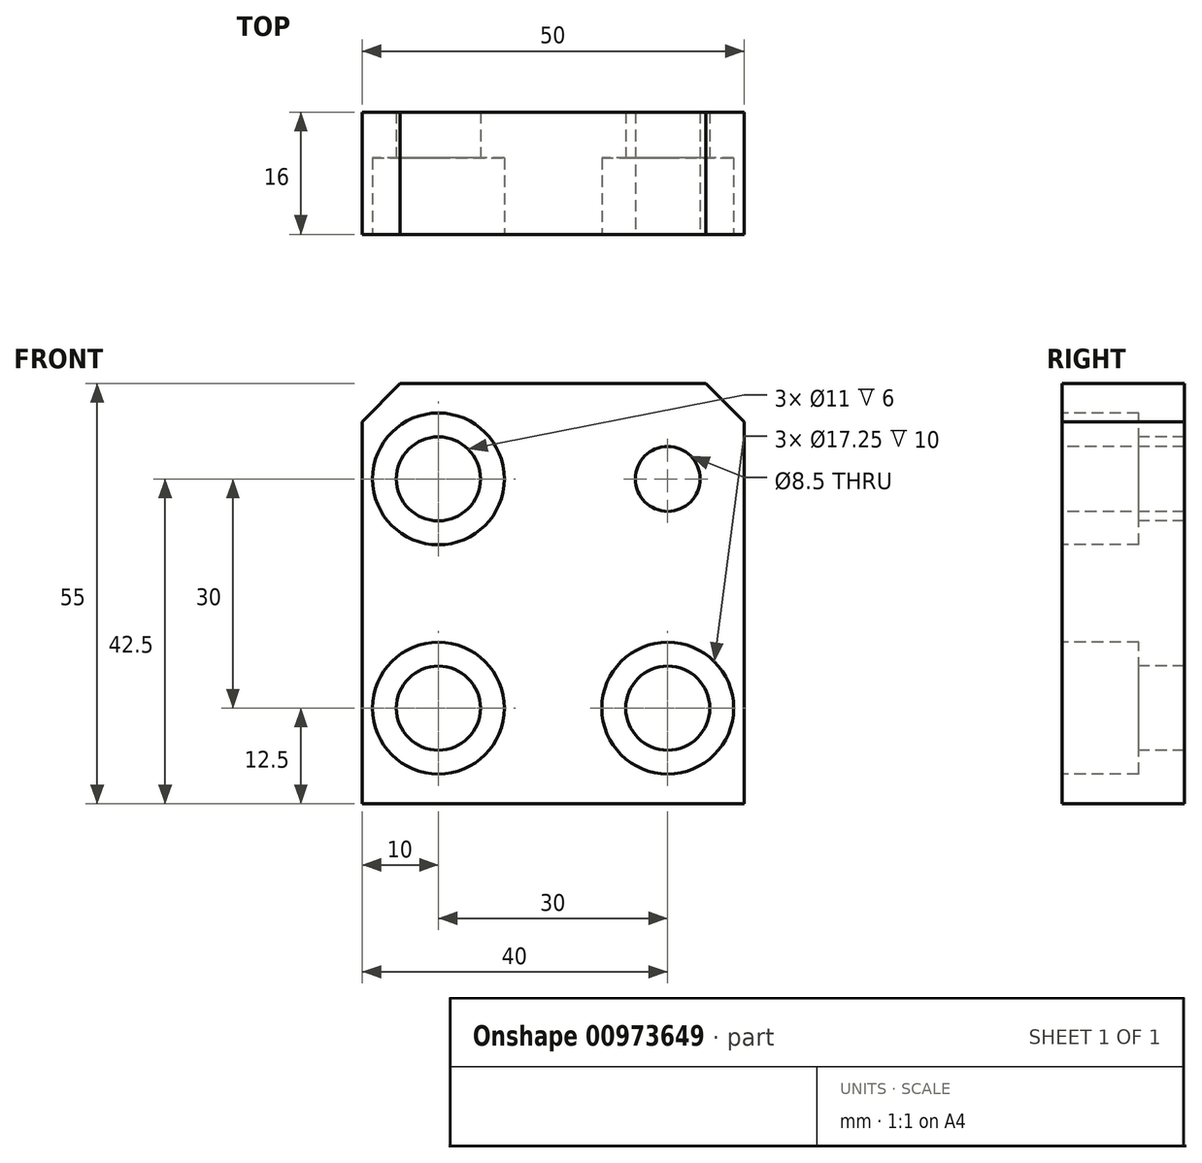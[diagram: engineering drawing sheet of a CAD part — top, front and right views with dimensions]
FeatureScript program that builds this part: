
annotation { "Feature Type Name" : "Feature", "Feature Type Description" : "" }
export const myFeature = defineFeature(function(context is Context, id is Id, definition is map)
    precondition{}
    {
        {
            var Q0;
            Q0=qCreatedBy(makeId("Front.planeOp"),FACE);
            var sketch = newSketch(context, id + "F0", { "sketchPlane" : qUnion([Q0])});
            skLineSegment(sketch, "E0.bottom", {"start": v(-25, -27.5) * mm, "end": v(25, -27.5) * mm});
            skLineSegment(sketch, "E0.top", {"start": v(-25, 27.5) * mm, "end": v(25, 27.5) * mm});
            skLineSegment(sketch, "E0.left", {"start": v(-25, -27.5) * mm, "end": v(-25, 27.5) * mm});
            skLineSegment(sketch, "E0.right", {"start": v(25, -27.5) * mm, "end": v(25, 27.5) * mm});
            skSolve(sketch);
        }
        {
            var Q0;
            Q0 = qSketchRegion(id + "F0", true);
            extrude(context, id + "F1", {"entities" : qUnion([Q0]), "oppositeDirection" : true, "depth" : 16 * mm, "offsetDistance" : 25.4 * mm});
        }
        {
            var Q0;
            Q0=makeQuery(id+"F1.opExtrude","CAP_FACE",FACE,{"disambiguationData":[OSD([sQuery(id+"F0.wireOp",EDGE,"E0.bottom"),sQuery(id+"F0.wireOp",EDGE,"E0.top"),sQuery(id+"F0.wireOp",EDGE,"E0.left"),sQuery(id+"F0.wireOp",EDGE,"E0.right")])],"isStart":true});
            var sketch = newSketch(context, id + "F2", { "sketchPlane" : qUnion([Q0])});
            skPoint(sketch, "E1", {"position": v(-15, 15) * mm});
            skPoint(sketch, "E2", {"position": v(-15, -15) * mm});
            skPoint(sketch, "E3", {"position": v(15, -15) * mm});
            skSolve(sketch);
        }
        {
            var Q0;
            Q0=sQuery(id+"F2.wireOp",VERTEX,"E1");
            var Q1;
            Q1=sQuery(id+"F2.wireOp",VERTEX,"E2");
            var Q2;
            Q2=sQuery(id+"F2.wireOp",VERTEX,"E3");
            var Q3;
            Q3=makeQuery(id+"F1.opExtrude","SWEPT_BODY",BODY,{"disambiguationData":[OSD([sQuery(id+"F0.wireOp",EDGE,"E0.bottom"),sQuery(id+"F0.wireOp",EDGE,"E0.top"),sQuery(id+"F0.wireOp",EDGE,"E0.left"),sQuery(id+"F0.wireOp",EDGE,"E0.right")])]});
            hole(context, id + "F3", {"style" : HoleStyle.C_BORE, "endStyle" : HoleEndStyle.THROUGH, "standardTappedOrClearance" : lookupTablePath({ "fit" : "Normal", "standard" : "ISO", "size" : "M10", "type" : "Clearance" }), "standardBlindInLast" : lookupTablePath({ "fit" : "Normal", "standard" : "ISO", "engagement" : "75%", "pitch" : "1.5 mm", "size" : "M10", "type" : "Clearance & tapped" }), "holeDiameter" : 11 * mm, "cBoreDiameter" : 17.25 * mm, "cBoreDepth" : 10 * mm, "majorDiameter" : 10 * mm, "isTappedThrough" : true, "tappedDepth" : 12.7 * mm, "tapClearance" : 3, "startFromSketch" : true, "locations" : qUnion([Q0, Q1, Q2]), "scope" : qUnion([Q3])});
        }
        {
            var Q0;
            Q0=makeQuery(id+"F1.opExtrude","CAP_FACE",FACE,{"disambiguationData":[OSD([sQuery(id+"F0.wireOp",EDGE,"E0.bottom"),sQuery(id+"F0.wireOp",EDGE,"E0.top"),sQuery(id+"F0.wireOp",EDGE,"E0.left"),sQuery(id+"F0.wireOp",EDGE,"E0.right")])],"isStart":true});
            var sketch = newSketch(context, id + "F4", { "sketchPlane" : qUnion([Q0])});
            skPoint(sketch, "E4", {"position": v(15, 15) * mm});
            skSolve(sketch);
        }
        {
            var Q0;
            Q0=sQuery(id+"F4.wireOp",VERTEX,"E4");
            var Q1;
            Q1=makeQuery(id+"F1.opExtrude","SWEPT_BODY",BODY,{"disambiguationData":[OSD([sQuery(id+"F0.wireOp",EDGE,"E0.bottom"),sQuery(id+"F0.wireOp",EDGE,"E0.top"),sQuery(id+"F0.wireOp",EDGE,"E0.left"),sQuery(id+"F0.wireOp",EDGE,"E0.right")])]});
            hole(context, id + "F5", {"style" : HoleStyle.SIMPLE, "endStyle" : HoleEndStyle.THROUGH, "standardTappedOrClearance" : lookupTablePath({ "standard" : "ISO", "engagement" : "75%", "pitch" : "1.5 mm", "size" : "M10", "type" : "Tapped" }), "standardBlindInLast" : lookupTablePath({ "standard" : "ISO", "fit" : "Normal", "engagement" : "75%", "pitch" : "1.5 mm", "size" : "M10", "type" : "Clearance & tapped" }), "holeDiameter" : 8.5 * mm, "majorDiameter" : 10 * mm, "showTappedDepth" : true, "isTappedThrough" : true, "tappedDepth" : 12.7 * mm, "tapClearance" : 3, "startFromSketch" : true, "locations" : qUnion([Q0]), "scope" : qUnion([Q1])});
        }
        {
            var Q0;
            Q0=makeQuery(id+"F1.opExtrude","SWEPT_EDGE",EDGE,{"disambiguationData":[OSD([sQuery(id+"F0.wireOp",EDGE,"E0.top"),sQuery(id+"F0.wireOp",EDGE,"E0.left")])]});
            var Q1;
            Q1=makeQuery(id+"F1.opExtrude","SWEPT_EDGE",EDGE,{"disambiguationData":[OSD([sQuery(id+"F0.wireOp",EDGE,"E0.top"),sQuery(id+"F0.wireOp",EDGE,"E0.right")])]});
            chamfer(context, id + "F6", {"entities" : qUnion([Q0, Q1]), "width" : 5 * mm, "tangentPropagation" : true});
        }
    });
